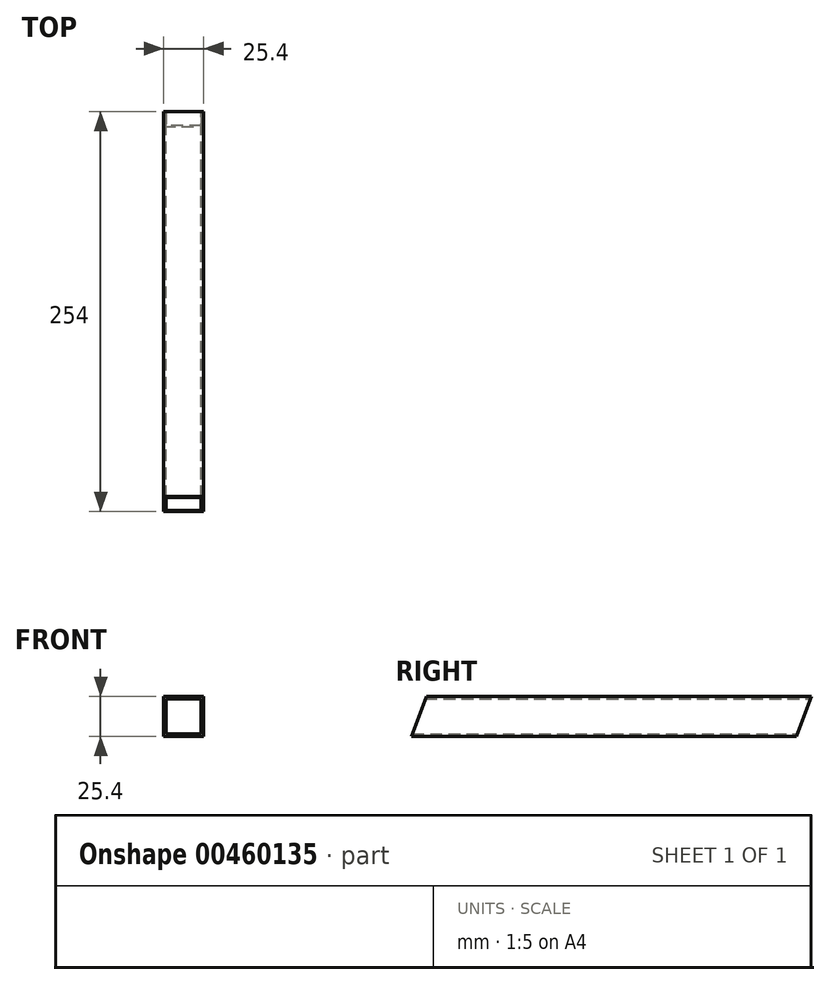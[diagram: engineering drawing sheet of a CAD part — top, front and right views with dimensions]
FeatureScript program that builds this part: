
annotation { "Feature Type Name" : "Feature", "Feature Type Description" : "" }
export const myFeature = defineFeature(function(context is Context, id is Id, definition is map)
    precondition{}
    {
        {
            var Q0;
            Q0=qCreatedBy(makeId("Front.planeOp"),FACE);
            var sketch = newSketch(context, id + "F0", { "sketchPlane" : qUnion([Q0])});
            skLineSegment(sketch, "E0.bottom", {"start": v(12.7, 12.7) * mm, "end": v(-12.7, 12.7) * mm});
            skLineSegment(sketch, "E0.top", {"start": v(12.7, -12.7) * mm, "end": v(-12.7, -12.7) * mm});
            skLineSegment(sketch, "E0.left", {"start": v(12.7, 12.7) * mm, "end": v(12.7, -12.7) * mm});
            skLineSegment(sketch, "E0.right", {"start": v(-12.7, 12.7) * mm, "end": v(-12.7, -12.7) * mm});
            skPoint(sketch, "E0.middle", {"position": v(0, 0) * mm});
            skLineSegment(sketch, "E1.bottom", {"start": v(11.11, 11.11) * mm, "end": v(-11.11, 11.11) * mm});
            skLineSegment(sketch, "E1.top", {"start": v(11.11, -11.11) * mm, "end": v(-11.11, -11.11) * mm});
            skLineSegment(sketch, "E1.left", {"start": v(11.11, 11.11) * mm, "end": v(11.11, -11.11) * mm});
            skLineSegment(sketch, "E1.right", {"start": v(-11.11, 11.11) * mm, "end": v(-11.11, -11.11) * mm});
            skSolve(sketch);
        }
        {
            var Q0;
            Q0=makeQuery(id+"F0.imprint","IMPRINT",FACE,{"disambiguationData":[TD([[makeQuery(id+"F0.imprint","IMPRINT",EDGE,{"derivedFrom":sQuery(id+"F0.wireOp",EDGE,"E0.bottom")}),1.0]])]});
            extrude(context, id + "F1", {"entities" : qUnion([Q0]), "depth" : 254 * mm});
        }
        {
            var Q0;
            Q0=makeQuery(id+"F1.opExtrude","CAP_EDGE",EDGE,{"disambiguationData":[OSD([sQuery(id+"F0.wireOp",EDGE,"E0.bottom")])],"isStart":false});
            chamfer(context, id + "F2", {"entities" : qUnion([Q0]), "chamferType" : ChamferType.OFFSET_ANGLE, "width" : 25.4 * mm, "oppositeDirection" : false, "angle" : 20.5 * degree, "tangentPropagation" : true});
        }
        {
            var Q0;
            Q0=makeQuery(id+"F1.opExtrude","CAP_EDGE",EDGE,{"disambiguationData":[OSD([sQuery(id+"F0.wireOp",EDGE,"E0.top")])],"isStart":true});
            chamfer(context, id + "F3", {"entities" : qUnion([Q0]), "chamferType" : ChamferType.OFFSET_ANGLE, "width" : 25.4 * mm, "oppositeDirection" : false, "angle" : 20.5 * degree, "tangentPropagation" : true});
        }
    });
